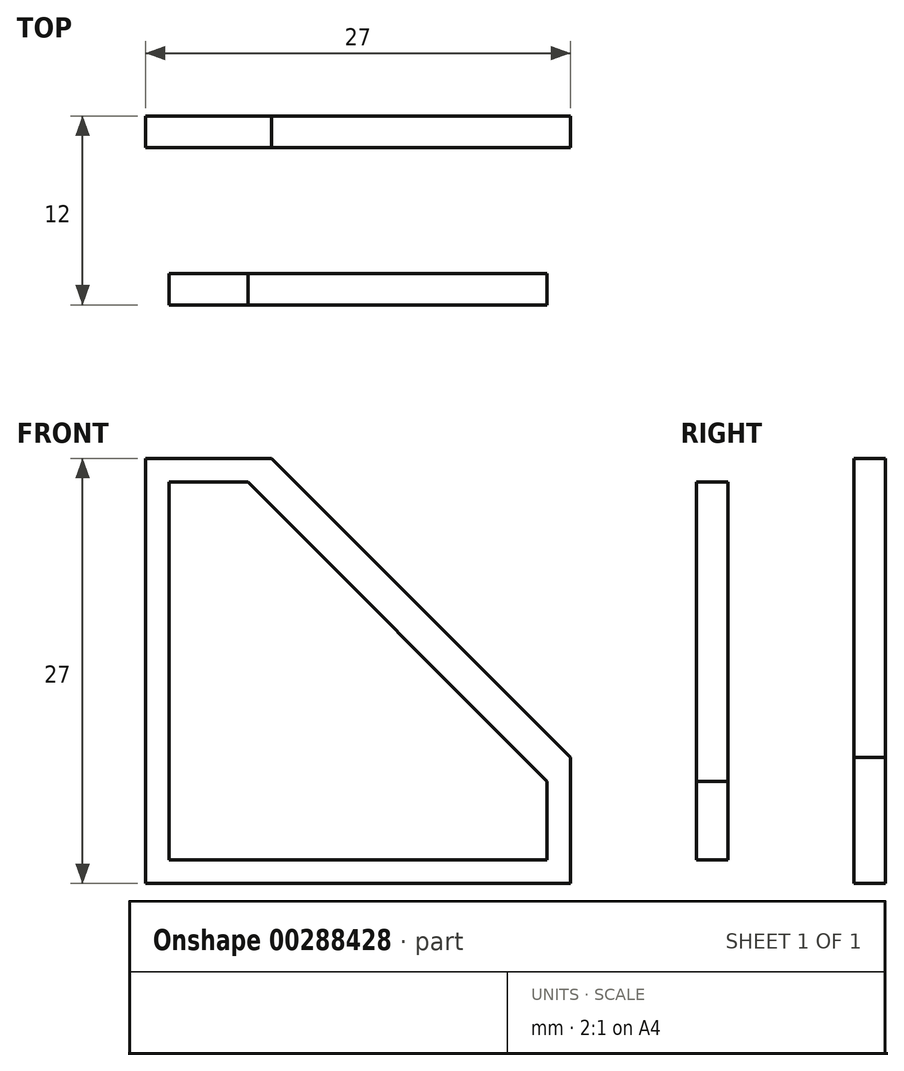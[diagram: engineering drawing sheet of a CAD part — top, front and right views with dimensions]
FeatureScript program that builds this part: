
annotation { "Feature Type Name" : "Feature", "Feature Type Description" : "" }
export const myFeature = defineFeature(function(context is Context, id is Id, definition is map)
    precondition{}
    {
        {
            var Q0;
            Q0=qCreatedBy(makeId("Front.planeOp"),FACE);
            var sketch = newSketch(context, id + "F0", { "sketchPlane" : qUnion([Q0])});
            skLineSegment(sketch, "E0.bottom", {"start": v(13.5, -13.5) * mm, "end": v(-13.5, -13.5) * mm});
            skLineSegment(sketch, "E0.top", {"start": v(-5.5, 13.5) * mm, "end": v(-13.5, 13.5) * mm});
            skLineSegment(sketch, "E0.left", {"start": v(13.5, -13.5) * mm, "end": v(13.5, -5.5) * mm});
            skLineSegment(sketch, "E0.right", {"start": v(-13.5, -13.5) * mm, "end": v(-13.5, 13.5) * mm});
            skPoint(sketch, "E0.middle", {"position": v(0, 0) * mm});
            skLineSegment(sketch, "E1", {"start": v(-5.5, 13.5) * mm, "end": v(13.5, -5.5) * mm});
            skPoint(sketch, "E2.orphan", {"position": v(13.5, 13.5) * mm});
            skSolve(sketch);
        }
        {
            var Q0;
            Q0=makeQuery(id+"F0.imprint","IMPRINT",FACE,{"disambiguationData":[TD([[makeQuery(id+"F0.imprint","IMPRINT",EDGE,{"derivedFrom":sQuery(id+"F0.wireOp",EDGE,"E0.bottom")}),-1.0]])]});
            extrude(context, id + "F1", {"entities" : qUnion([Q0]), "depth" : 2 * mm});
        }
        {
            var Q0;
            Q0=qCreatedBy(makeId("Front.planeOp"),FACE);
            cPlane(context, id + "F2", {"entities" : qUnion([Q0]), "cplaneType" : CPlaneType.OFFSET, "offset" : 10 * mm, "width" : 150 * mm, "height" : 150 * mm});
        }
        {
            var Q0;
            Q0=qCreatedBy(id+"F2.planeOp",FACE);
            var sketch = newSketch(context, id + "F3", { "sketchPlane" : qUnion([Q0])});
            skLineSegment(sketch, "E3.bottom", {"start": v(12, -12) * mm, "end": v(-12, -12) * mm});
            skLineSegment(sketch, "E3.top", {"start": v(-7, 12) * mm, "end": v(-12, 12) * mm});
            skLineSegment(sketch, "E3.left", {"start": v(12, -12) * mm, "end": v(12, -7) * mm});
            skLineSegment(sketch, "E3.right", {"start": v(-12, -12) * mm, "end": v(-12, 12) * mm});
            skPoint(sketch, "E3.middle", {"position": v(0, 0) * mm});
            skLineSegment(sketch, "E4", {"start": v(-7, 12) * mm, "end": v(12, -7) * mm});
            skPoint(sketch, "E5.orphan", {"position": v(12, 12) * mm});
            skSolve(sketch);
        }
        {
            var Q0;
            Q0=makeQuery(id+"F3.imprint","IMPRINT",FACE,{"disambiguationData":[TD([[makeQuery(id+"F3.imprint","IMPRINT",EDGE,{"derivedFrom":sQuery(id+"F3.wireOp",EDGE,"E3.bottom")}),-1.0]])]});
            extrude(context, id + "F4", {"entities" : qUnion([Q0]), "depth" : 2 * mm});
        }
    });
